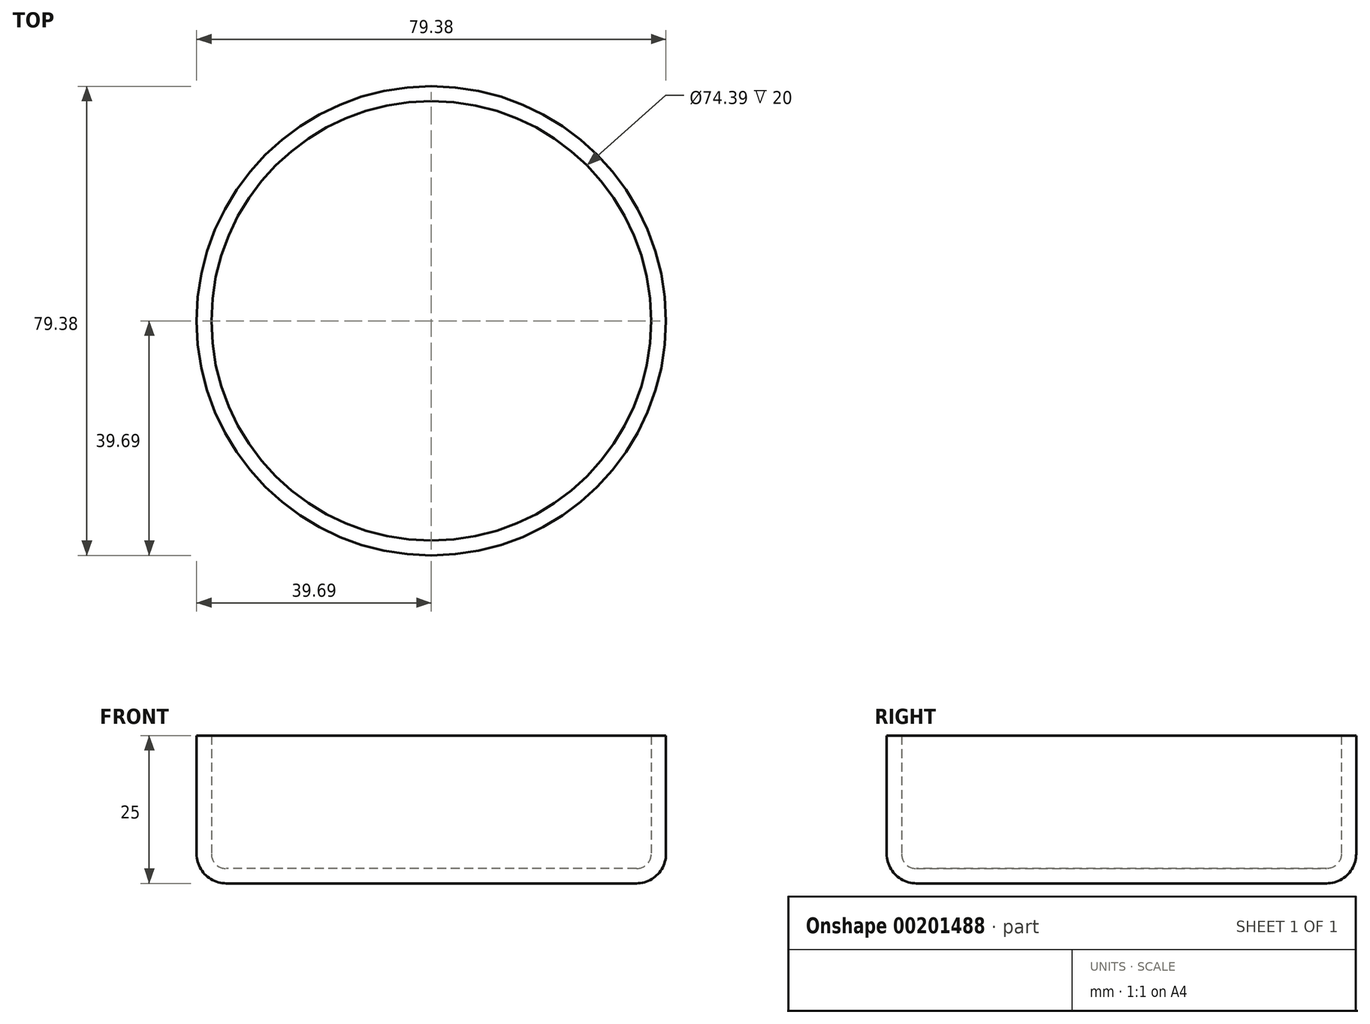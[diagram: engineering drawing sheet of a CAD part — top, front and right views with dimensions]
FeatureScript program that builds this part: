
annotation { "Feature Type Name" : "Feature", "Feature Type Description" : "" }
export const myFeature = defineFeature(function(context is Context, id is Id, definition is map)
    precondition{}
    {
        {
            var Q0;
            Q0=qCreatedBy(makeId("Top.planeOp"),FACE);
            var sketch = newSketch(context, id + "F0", { "sketchPlane" : qUnion([Q0])});
            skCircle(sketch, "E0", {"center": v(0, 0) * mm, "radius": 39.7 * mm});
            skSolve(sketch);
        }
        {
            var Q0;
            Q0=makeQuery(id+"F0.imprint","IMPRINT",FACE,{"disambiguationData":[TD([[makeQuery(id+"F0.imprint","IMPRINT",EDGE,{"derivedFrom":sQuery(id+"F0.wireOp",EDGE,"E0")}),1.0]])]});
            extrude(context, id + "F1", {"entities" : qUnion([Q0]), "depth" : 25 * mm});
        }
        {
            var Q0;
            Q0=makeQuery(id+"F1.opExtrude","CAP_EDGE",EDGE,{"disambiguationData":[OSD([sQuery(id+"F0.wireOp",EDGE,"E0")])],"isStart":true});
            fillet(context, id + "F2", {"entities" : qUnion([Q0]), "radius" : 5 * mm, "tangentPropagation" : true, "allowEdgeOverflow" : false});
        }
        {
            var Q0;
            Q0=makeQuery(id+"F1.opExtrude","CAP_FACE",FACE,{"disambiguationData":[OSD([sQuery(id+"F0.wireOp",EDGE,"E0")])],"isStart":false});
            shell(context, id + "F3", {"entities" : qUnion([Q0]), "thickness" : 2.5 * mm});
        }
    });
